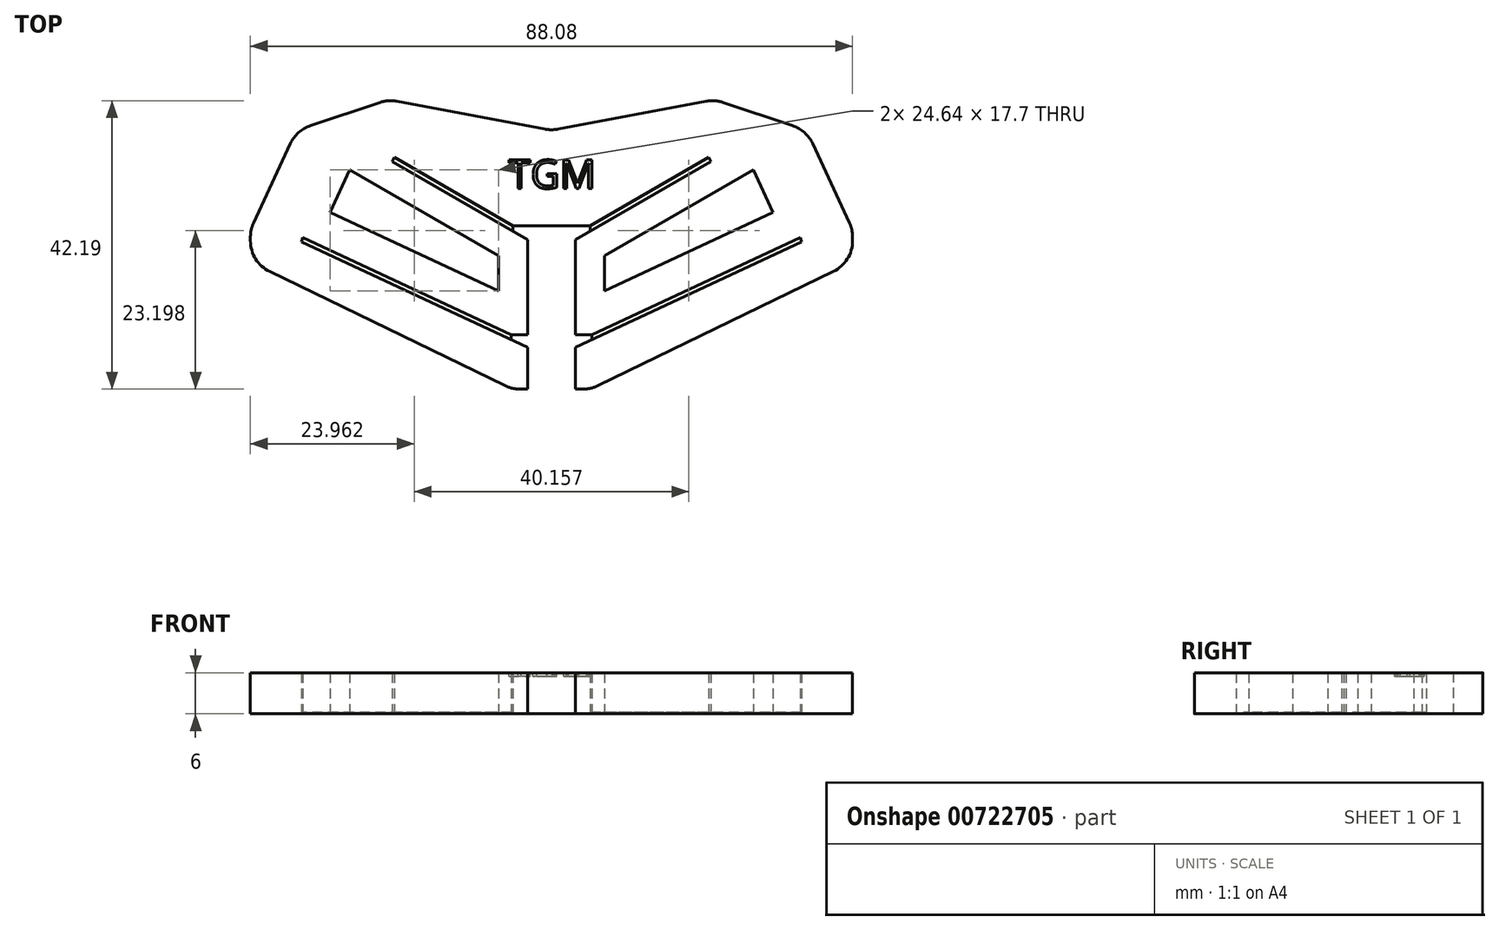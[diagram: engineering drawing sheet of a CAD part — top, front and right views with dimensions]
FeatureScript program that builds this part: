
annotation { "Feature Type Name" : "Feature", "Feature Type Description" : "" }
export const myFeature = defineFeature(function(context is Context, id is Id, definition is map)
    precondition{}
    {
        {
            var Q0;
            Q0=qCreatedBy(makeId("Top.planeOp"),FACE);
            var sketch = newSketch(context, id + "F0", { "sketchPlane" : qUnion([Q0])});
            skLineSegment(sketch, "E0", {"start": v(-8.5, 0) * mm, "end": v(-44.04, 17.24) * mm});
            skLineSegment(sketch, "E1", {"start": v(-44.04, 22) * mm, "end": v(-37.3, 36.53) * mm});
            skLineSegment(sketch, "E2", {"start": v(0, 24.01) * mm, "end": v(0, 22.58) * mm});
            skLineSegment(sketch, "E3", {"start": v(0, 22.58) * mm, "end": v(-3.5, 22.58) * mm});
            skLineSegment(sketch, "E4", {"start": v(-5.67, 22.58) * mm, "end": v(-22.99, 32.58) * mm});
            skLineSegment(sketch, "E5", {"start": v(-22.99, 32.58) * mm, "end": v(-23.3, 31.96) * mm});
            skLineSegment(sketch, "E6", {"start": v(-23.3, 31.96) * mm, "end": v(-3.5, 20.53) * mm});
            skLineSegment(sketch, "E7", {"start": v(-7.76, 18.17) * mm, "end": v(-29.51, 30.73) * mm});
            skLineSegment(sketch, "E8", {"start": v(-29.51, 30.73) * mm, "end": v(-32.4, 24.52) * mm});
            skLineSegment(sketch, "E9", {"start": v(-32.4, 24.52) * mm, "end": v(-7.76, 13.03) * mm});
            skLineSegment(sketch, "E10", {"start": v(-5.9, 6.64) * mm, "end": v(-36.37, 20.86) * mm});
            skLineSegment(sketch, "E11", {"start": v(-36.58, 20.19) * mm, "end": v(-36.37, 20.86) * mm});
            skLineSegment(sketch, "E12", {"start": v(-36.58, 20.19) * mm, "end": v(-3.5, 4.76) * mm});
            skLineSegment(sketch, "E13", {"start": v(-7.76, 18.17) * mm, "end": v(-7.76, 13.03) * mm});
            skLineSegment(sketch, "E14.trimOffspring", {"start": v(-3.5, 20.53) * mm, "end": v(-3.5, 6.64) * mm});
            skLineSegment(sketch, "E15.trimOffspring", {"start": v(-3.5, 4.76) * mm, "end": v(-3.5, 0) * mm});
            skLineSegment(sketch, "E16", {"start": v(0, 25.05) * mm, "end": v(0, 24.01) * mm});
            skLineSegment(sketch, "E17", {"start": v(-23.87, 41.02) * mm, "end": v(-37.3, 36.53) * mm});
            skLineSegment(sketch, "E18", {"start": v(-23.87, 41.02) * mm, "end": v(0, 36.53) * mm});
            skLineSegment(sketch, "E19", {"start": v(0, 36.53) * mm, "end": v(0, 25.05) * mm});
            skLineSegment(sketch, "E20", {"start": v(-44.04, 22) * mm, "end": v(-44.04, 17.24) * mm});
            skLineSegment(sketch, "E21", {"start": v(-5.9, 6.64) * mm, "end": v(-3.5, 6.64) * mm});
            skLineSegment(sketch, "E22", {"start": v(-3.5, 22.58) * mm, "end": v(-5.67, 22.58) * mm});
            skPoint(sketch, "E23.orphan", {"position": v(-3.5, 21.33) * mm});
            skPoint(sketch, "E24.orphan", {"position": v(-3.5, 5.53) * mm});
            skLineSegment(sketch, "E25", {"start": v(-5.67, 22.58) * mm, "end": v(-5.67, 21.78) * mm});
            skLineSegment(sketch, "E26", {"start": v(-5.9, 6.64) * mm, "end": v(-5.9, 5.88) * mm});
            skLineSegment(sketch, "E27", {"start": v(-8.5, 0) * mm, "end": v(-5.78, -1.32) * mm});
            skLineSegment(sketch, "E28", {"start": v(-5.78, -1.32) * mm, "end": v(-3.5, -1.32) * mm});
            skLineSegment(sketch, "E29", {"start": v(-3.5, -1.32) * mm, "end": v(-3.5, 0) * mm});
            skSolve(sketch);
        }
        {
            var Q0;
            Q0=makeQuery(id+"F0.imprint","IMPRINT",FACE,{"disambiguationData":[TD([[makeQuery(id+"F0.imprint","IMPRINT",EDGE,{"derivedFrom":sQuery(id+"F0.wireOp",EDGE,"E0")}),-1.0]])]});
            extrude(context, id + "F1", {"entities" : qUnion([Q0]), "depth" : 6 * mm, "offsetDistance" : 25 * mm});
        }
        {
            var Q0;
            Q0=makeQuery(id+"F0.imprint","IMPRINT",FACE,{"disambiguationData":[TD([[makeQuery(id+"F0.imprint","IMPRINT",EDGE,{"derivedFrom":sQuery(id+"F0.wireOp",EDGE,"E4")}),1.0]])]});
            var Q1;
            Q1=makeQuery(id+"F0.imprint","IMPRINT",FACE,{"disambiguationData":[TD([[makeQuery(id+"F0.imprint","IMPRINT",EDGE,{"derivedFrom":sQuery(id+"F0.wireOp",EDGE,"E10")}),1.0]])]});
            extrude(context, id + "F2", {"entities" : qUnion([Q0, Q1]), "operationType" : NewBodyOperationType.ADD, "depth" : .2 * mm, "offsetDistance" : 25 * mm});
        }
        {
            var Q0;
            Q0=makeQuery(id+"F1.opExtrude","SWEPT_EDGE",EDGE,{"disambiguationData":[OSD([sQuery(id+"F0.wireOp",EDGE,"E0"),sQuery(id+"F0.wireOp",EDGE,"E20")])]});
            var Q1;
            Q1=makeQuery(id+"F1.opExtrude","SWEPT_EDGE",EDGE,{"disambiguationData":[OSD([sQuery(id+"F0.wireOp",EDGE,"E1"),sQuery(id+"F0.wireOp",EDGE,"E20")])]});
            var Q2;
            Q2=makeQuery(id+"F1.opExtrude","SWEPT_EDGE",EDGE,{"disambiguationData":[OSD([sQuery(id+"F0.wireOp",EDGE,"E1"),sQuery(id+"F0.wireOp",EDGE,"E17")])]});
            var Q3;
            Q3=makeQuery(id+"F1.opExtrude","SWEPT_EDGE",EDGE,{"disambiguationData":[OSD([sQuery(id+"F0.wireOp",EDGE,"E17"),sQuery(id+"F0.wireOp",EDGE,"E18")])]});
            var Q4;
            Q4=makeQuery(id+"F1.opExtrude","SWEPT_EDGE",EDGE,{"disambiguationData":[OSD([sQuery(id+"F0.wireOp",EDGE,"E27"),sQuery(id+"F0.wireOp",EDGE,"E28")])]});
            fillet(context, id + "F3", {"entities" : qUnion([Q0, Q1, Q2, Q3, Q4]), "radius" : 5 * mm, "tangentPropagation" : true, "allowEdgeOverflow" : false});
        }
        {
            var Q0;
            Q0=makeQuery(id+"F1.opExtrude","SWEPT_BODY",BODY,{"disambiguationData":[OSD([sQuery(id+"F0.wireOp",EDGE,"s68BUaBl-pctZ-WALU-i0se-HPyoojUsH6RM"),sQuery(id+"F0.wireOp",EDGE,"E0"),sQuery(id+"F0.wireOp",EDGE,"E1"),sQuery(id+"F0.wireOp",EDGE,"dslSHWXx-QNfY-dr7z-3vz7-gSjychyStgwG"),sQuery(id+"F0.wireOp",EDGE,"Py8xkcvr-5UOc-NVMb-QGT7-cQ4YutF3A1W0"),sQuery(id+"F0.wireOp",EDGE,"RdXJCQVM-t77z-hnpy-P4fF-eQJG8YKpdsMY"),sQuery(id+"F0.wireOp",EDGE,"sJrRfMdK-fnZH-ZeSw-Nd8b-FGg4ionJENBF"),sQuery(id+"F0.wireOp",EDGE,"mjDraEgt-OX3M-t9fj-jP6J-1X2QuJWmQcKb"),sQuery(id+"F0.wireOp",EDGE,"JPigT3Yn-AHkZ-Jk0b-Ix59-GkdeApKjpKik"),sQuery(id+"F0.wireOp",EDGE,"j61hzGhU-BBvW-fAdn-8j4O-Emwpdaet7zdu"),sQuery(id+"F0.wireOp",EDGE,"E2"),sQuery(id+"F0.wireOp",EDGE,"E3"),sQuery(id+"F0.wireOp",EDGE,"t2e31gEi-wCQ3-jEsl-YgTP-jqKrsm8FAa0U"),sQuery(id+"F0.wireOp",EDGE,"E4"),sQuery(id+"F0.wireOp",EDGE,"E5"),sQuery(id+"F0.wireOp",EDGE,"E6"),sQuery(id+"F0.wireOp",EDGE,"E7"),sQuery(id+"F0.wireOp",EDGE,"E8"),sQuery(id+"F0.wireOp",EDGE,"E9"),sQuery(id+"F0.wireOp",EDGE,"E10"),sQuery(id+"F0.wireOp",EDGE,"E11"),sQuery(id+"F0.wireOp",EDGE,"E12"),sQuery(id+"F0.wireOp",EDGE,"E13"),sQuery(id+"F0.wireOp",EDGE,"E14.trimOffspring"),sQuery(id+"F0.wireOp",EDGE,"E15.trimOffspring")])]});
            var Q1;
            Q1=qCreatedBy(makeId("Right.planeOp"),FACE);
            mirror(context, id + "F4", {"operationType" : NewBodyOperationType.ADD, "entities" : qUnion([Q0]), "mirrorPlane" : qUnion([Q1])});
        }
        {
            var Q0;
            {var subQ0=makeQuery(id+"F1.opExtrude","CAP_FACE",FACE,{"disambiguationData":[OSD([sQuery(id+"F0.wireOp",EDGE,"E0"),sQuery(id+"F0.wireOp",EDGE,"E1"),sQuery(id+"F0.wireOp",EDGE,"E2"),sQuery(id+"F0.wireOp",EDGE,"E3"),sQuery(id+"F0.wireOp",EDGE,"E4"),sQuery(id+"F0.wireOp",EDGE,"E5"),sQuery(id+"F0.wireOp",EDGE,"E6"),sQuery(id+"F0.wireOp",EDGE,"E7"),sQuery(id+"F0.wireOp",EDGE,"E8"),sQuery(id+"F0.wireOp",EDGE,"E9"),sQuery(id+"F0.wireOp",EDGE,"E10"),sQuery(id+"F0.wireOp",EDGE,"E11"),sQuery(id+"F0.wireOp",EDGE,"E12"),sQuery(id+"F0.wireOp",EDGE,"E13"),sQuery(id+"F0.wireOp",EDGE,"E14.trimOffspring"),sQuery(id+"F0.wireOp",EDGE,"E15.trimOffspring"),sQuery(id+"F0.wireOp",EDGE,"E16"),sQuery(id+"F0.wireOp",EDGE,"E17"),sQuery(id+"F0.wireOp",EDGE,"E18"),sQuery(id+"F0.wireOp",EDGE,"E19"),sQuery(id+"F0.wireOp",EDGE,"E20"),sQuery(id+"F0.wireOp",EDGE,"E21"),sQuery(id+"F0.wireOp",EDGE,"E22"),sQuery(id+"F0.wireOp",EDGE,"E27"),sQuery(id+"F0.wireOp",EDGE,"E28"),sQuery(id+"F0.wireOp",EDGE,"E29")])],"isStart":false});Q0=makeQuery(id+"F4.boolean.opBoolean","MERGE",FACE,{"derivedFrom":[subQ0,makeQuery(id+"F4.opPattern","COPY",FACE,{"derivedFrom":subQ0,"instanceName":"1"})]});}
            var sketch = newSketch(context, id + "F5", { "sketchPlane" : qUnion([Q0])});
            skText(sketch, "E30", { "text": "TGM", "fontName": "OpenSans-Regular.ttf"});
            const initialGuessF5  = {"E30": [-0.00628, 0.02803, 1, 0, 0.0042]};
            skSetInitialGuess(sketch, initialGuessF5);
            skSolve(sketch);
        }
        {
            var Q0;
            Q0 = qSketchRegion(id + "F5", true);
            extrude(context, id + "F6", {"entities" : qUnion([Q0]), "operationType" : NewBodyOperationType.REMOVE, "oppositeDirection" : true, "depth" : .5 * mm, "offsetDistance" : 25 * mm});
        }
        {
            var Q0;
            {var subQ0=makeQuery(id+"F1.opExtrude","SWEPT_EDGE",EDGE,{"disambiguationData":[OSD([sQuery(id+"F0.wireOp",EDGE,"E18"),sQuery(id+"F0.wireOp",EDGE,"E19")])]});Q0=makeQuery(id+"F4.boolean.opBoolean","MERGE",EDGE,{"derivedFrom":[subQ0,makeQuery(id+"F4.opPattern","COPY",EDGE,{"derivedFrom":subQ0,"instanceName":"1"})]});}
            fillet(context, id + "F7", {"entities" : qUnion([Q0]), "radius" : 5 * mm, "tangentPropagation" : true, "allowEdgeOverflow" : false});
        }
    });
